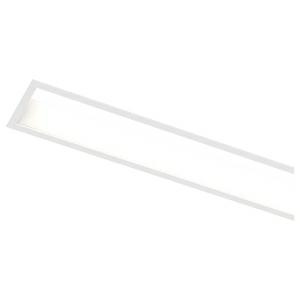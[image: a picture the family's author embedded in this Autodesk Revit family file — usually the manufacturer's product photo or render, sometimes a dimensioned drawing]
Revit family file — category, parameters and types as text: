
# Revit family: groove_l_1460_eb_led_26w_1704lm_3000k_cri80_230-2050_2e74
name_source: partatom
category: Leuchten
revit_build: Autodesk Revit 2016 (Build: 20190508_0715(x64)
units: mm (PartAtom-declared; Revit-internal decimal feet)

## family parameters
Basisbauteil = Fläche
Beim Laden mit Abzugskörper schneiden = Nein
Bemaßung runder Anschluss = Durchmesser verwenden
Gemeinsam genutzt = Nein
Lichtquelle = Nein
Raumberechnungspunkt = Nein
Teiletyp = Normal

## types (1)
- 230-2050- (5 x LED, 710 lm, 5.1 W, 3000K)
    Beschreibung = The recessed luminaire GROOVE from the familiy GROOVE consists of aluminum-extruded profile. Charming SOFT-EDGE design ensure unparalleled styling. The ballast is integrated and allows for an operation with 220-240V (50.60Hz). GROOVE (# 230-2050) ist not dimmable (on/off). The luminaire with direct illumination and corresponds to protection class SK1 at IP20.
    CIE Flux Codes = 59 87 97 100 49
    Color Rendering = 1B/80…89
    Color Temperature = 3000K
    Height = 0 mm  [stored 0 ft]
    Hersteller = Prolicht
    Lamp Light Flux = 710 lm
    Lamp Power = 5.1 W
    Lamp count = 5
    Lampe = 5 x LED
    Length = 1460 mm
    Luminous efficacy = 67 lm/W
    ModVariant = Nein
    Modell = 230-2050
    Mounting Place = Ceiling
    Mounting Type = Recessed
    Number of Poles = 1
    OnlyDefault = Ja
    Power Factor = 1
    Product Name = GROOVE L=1460 EB LED 26W 1704lm 3000K CRI80
    Product group = Recessed profile lights
    ProductGroupID = 423
    Protection Class = Protection class
    Protection Degree = Degree of protection
    RLX_Detail_Level = 1
    RlxData = <blob elided: 168057 chars, md5=9a2bbfbb>
    Scheinlast = 26 VA
    Socket = socket
    Standby Power = 0 W
    System Light Flux = 1712 lm
    System Power = 26 W
    Typenbild = 230-2050.jpg
    URL = http://relux.com
    VarID = 230-2050-
    Voltage = 0 V
    Vorgabe-Ansicht = 1800 mm
    Weight = 0.00 kg
    Width = 92 mm

note: [stored X ft] marks values corroborated as IEEE doubles in the binary element streams (Revit-internal decimal feet)

## geometry (parser evidence)
native form markers: Blend x4, Sweep x13
no freeform markers — native parametric forms only
